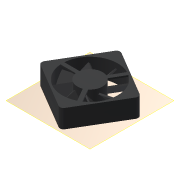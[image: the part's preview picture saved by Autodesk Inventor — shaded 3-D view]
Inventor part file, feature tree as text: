
AUTODESK INVENTOR PART (.ipt)
format: ipt  version: 2016 (Build 200138000, 138)  size: 201,216 bytes
history: native  units: mm
features: extrude x5, sketch x5, reference x4, pattern_circular x2, plane x1, projected_geometry x1
ambient origin geometry x8: Origin, YZ Plane, XZ Plane, XY Plane, X Axis, Y Axis, Z Axis, Center Point
bodies: Solid1 (feature_tree), Solid2 (feature_tree)
feature tree (18):
  plane  "Work Plane1"
  extrude  "Extrusion1"  Depth=5.0mm
  extrude  "Extrusion2"  Depth=25.0mm
  extrude  "Extrusion3"  Depth=25.0mm TaperAngle=0.0deg
  pattern_circular  "Circular Pattern1"  Count=3 Angle=360.0deg
  extrude  "Extrusion4"  Depth=2.0mm TaperAngle=0.0deg
  pattern_circular  "Circular Pattern2"  Count=8 Angle=360.0deg
  extrude  "Extrusion5"  Depth=80.0mm TaperAngle=0.0deg
  sketch  "Sketch1"  dims[d0=80.0mm d1=5.0mm]
  reference  "Reference1"
  reference  "Reference2"
  reference  "Reference3"
  reference  "Reference4"
  sketch  "Sketch2"  dims[d2=25.0mm d3=0.0mm d4=34.0mm]
  projected_geometry  "Projected Loop1"
  sketch  "Sketch3"  dims[d5=75.0mm d6=25.0mm d7=0.0mm]
  sketch  "Sketch4"  dims[d8=2.0mm d9=0.0mm d10=30.0mm d11=360.0deg]
  sketch  "Sketch5"  dims[d13=8.726646mm d14=2.0mm d15=0.0mm d16=80.0mm d17=360.0deg d19=40.0mm d20=0.0mm]
